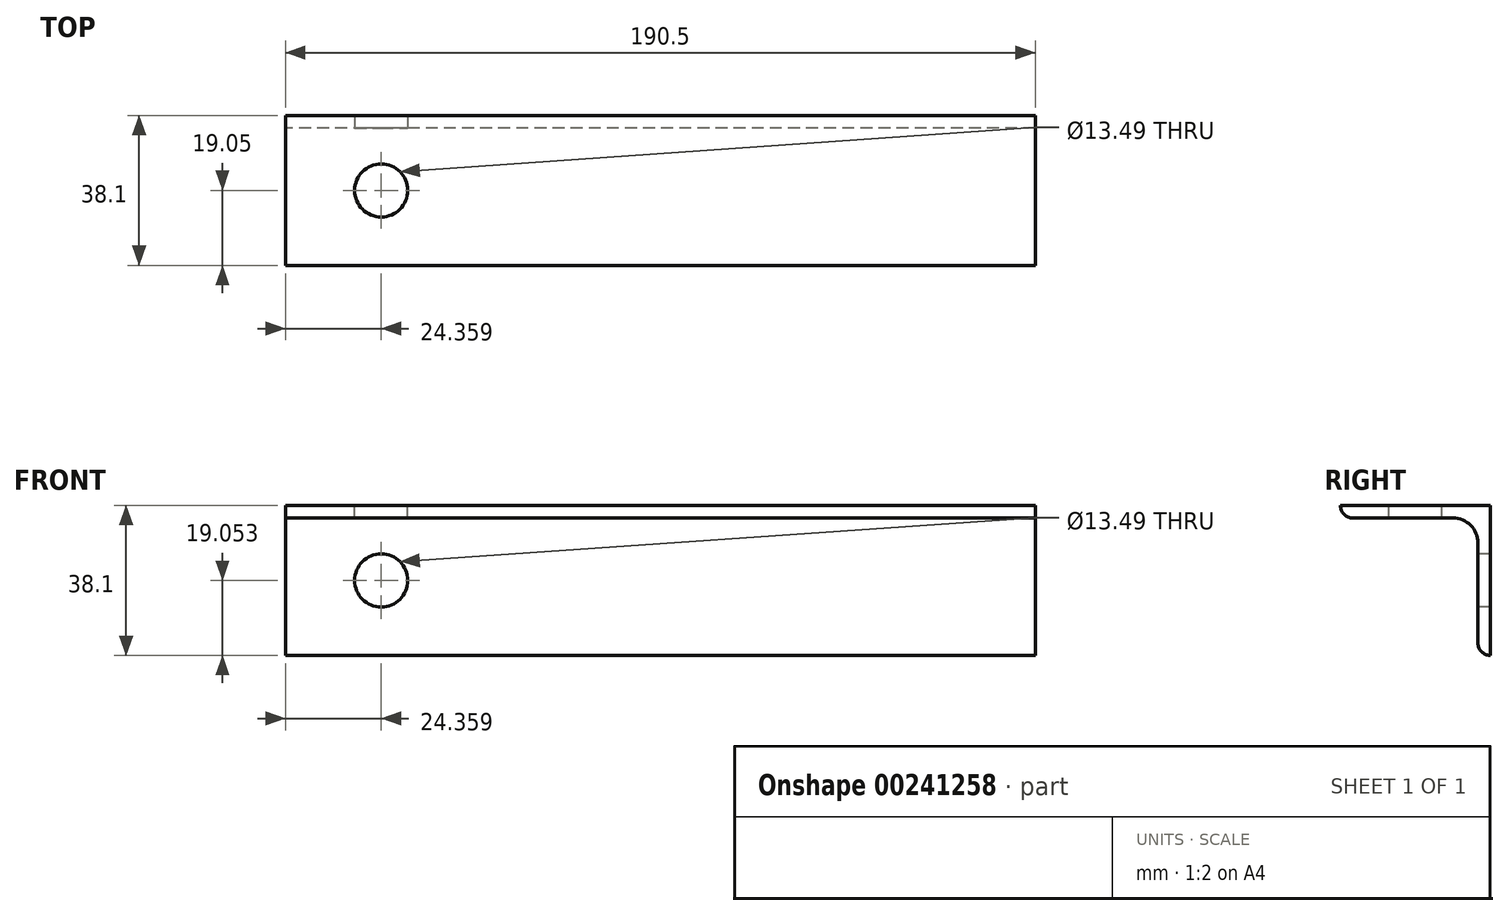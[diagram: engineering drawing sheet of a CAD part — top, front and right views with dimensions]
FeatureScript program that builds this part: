
annotation { "Feature Type Name" : "Feature", "Feature Type Description" : "" }
export const myFeature = defineFeature(function(context is Context, id is Id, definition is map)
    precondition{}
    {
        {
            var Q0;
            Q0=qCreatedBy(makeId("Right.planeOp"),FACE);
            var sketch = newSketch(context, id + "F0", { "sketchPlane" : qUnion([Q0])});
            skLineSegment(sketch, "E0", {"start": v(0, -7.2) * mm, "end": v(0, 30.9) * mm});
            skLineSegment(sketch, "E1", {"start": v(0, 30.9) * mm, "end": v(-38.1, 30.9) * mm});
            skLineSegment(sketch, "E2", {"start": v(-38.1, 30.9) * mm, "end": v(-38.1, 30.9) * mm});
            skLineSegment(sketch, "E3", {"start": v(-34.93, 27.73) * mm, "end": v(-9.52, 27.73) * mm});
            skLineSegment(sketch, "E4", {"start": v(-3.17, 21.38) * mm, "end": v(-3.17, -4.02) * mm});
            skLineSegment(sketch, "E5", {"start": v(-0.1, -7.19) * mm, "end": v(0, -7.2) * mm});
            skPoint(sketch, "E6.visualSharp", {"position": v(-3.17, -7.09) * mm});
            skArc(sketch, "E6.filletArc", {"start": v(-3.17, -4.02) * mm, "mid": v(-2.28, -6.22) * mm, "end": v(-0.1, -7.19) * mm});
            skPoint(sketch, "E7.visualSharp", {"position": v(-38.1, 27.73) * mm});
            skArc(sketch, "E7.filletArc", {"start": v(-38.1, 30.9) * mm, "mid": v(-37.17, 28.66) * mm, "end": v(-34.93, 27.73) * mm});
            skPoint(sketch, "E8.visualSharp", {"position": v(-3.17, 27.73) * mm});
            skArc(sketch, "E8.filletArc", {"start": v(-3.17, 21.38) * mm, "mid": v(-5.03, 25.87) * mm, "end": v(-9.52, 27.73) * mm});
            skSolve(sketch);
        }
        {
            var Q0;
            Q0=makeQuery(id+"F0.imprint","IMPRINT",FACE,{"disambiguationData":[TD([[makeQuery(id+"F0.imprint","IMPRINT",EDGE,{"derivedFrom":sQuery(id+"F0.wireOp",EDGE,"E0")}),1.0]])]});
            extrude(context, id + "F1", {"entities" : qUnion([Q0]), "depth" : 190.5 * mm});
        }
        {
            var Q0;
            Q0=makeQuery(id+"F1.opExtrude","SWEPT_BODY",BODY,{"disambiguationData":[OSD([sQuery(id+"F0.wireOp",EDGE,"E0"),sQuery(id+"F0.wireOp",EDGE,"E1"),sQuery(id+"F0.wireOp",EDGE,"E3"),sQuery(id+"F0.wireOp",EDGE,"E4"),sQuery(id+"F0.wireOp",EDGE,"E5"),sQuery(id+"F0.wireOp",EDGE,"E6.filletArc"),sQuery(id+"F0.wireOp",EDGE,"E7.filletArc"),sQuery(id+"F0.wireOp",EDGE,"E8.filletArc")])]});
            transform(context, id + "F2", {"entities" : qUnion([Q0]), "transformType" : TransformType.TRANSLATION_3D, "dx" : -137.16 * mm, "dy" : 0 * mm, "dz" : 1.52 * mm, "makeCopy" : false});
        }
        {
            var Q0;
            Q0=makeQuery(id+"F1.opExtrude","SWEPT_FACE",FACE,{"disambiguationData":[OSD([sQuery(id+"F0.wireOp",EDGE,"E4")])]});
            var sketch = newSketch(context, id + "F3", { "sketchPlane" : qUnion([Q0])});
            skCircle(sketch, "E9", {"center": v(-112.8, 13.38) * mm, "radius": 6.35 * mm});
            skLineSegment(sketch, "E10", {"start": v(-112.8, 13.38) * mm, "end": v(-137.16, 13.38) * mm});
            skLineSegment(sketch, "E11.bottom", {"start": v(-137.16, 22.9) * mm, "end": v(53.34, 22.9) * mm});
            skLineSegment(sketch, "E11.top", {"start": v(-137.16, -2.5) * mm, "end": v(53.34, -2.5) * mm});
            skLineSegment(sketch, "E11.left", {"start": v(-137.16, 22.9) * mm, "end": v(-137.16, -2.5) * mm});
            skLineSegment(sketch, "E11.right", {"start": v(53.34, 22.9) * mm, "end": v(53.34, -2.5) * mm});
            skSolve(sketch);
        }
        {
            var Q0;
            Q0=makeQuery(id+"F1.opExtrude","SWEPT_FACE",FACE,{"disambiguationData":[OSD([sQuery(id+"F0.wireOp",EDGE,"E1")])]});
            var sketch = newSketch(context, id + "F4", { "sketchPlane" : qUnion([Q0])});
            skCircle(sketch, "E12", {"center": v(-112.8, -19.05) * mm, "radius": 9.24 * mm});
            skSolve(sketch);
        }
        {
            var Q0;
            Q0=sQuery(id+"F4.wireOp",VERTEX,"E12.center");
            var Q1;
            Q1=makeQuery(id+"F1.opExtrude","SWEPT_BODY",BODY,{"disambiguationData":[OSD([sQuery(id+"F0.wireOp",EDGE,"E0"),sQuery(id+"F0.wireOp",EDGE,"E1"),sQuery(id+"F0.wireOp",EDGE,"E3"),sQuery(id+"F0.wireOp",EDGE,"E4"),sQuery(id+"F0.wireOp",EDGE,"E5"),sQuery(id+"F0.wireOp",EDGE,"E6.filletArc"),sQuery(id+"F0.wireOp",EDGE,"E7.filletArc"),sQuery(id+"F0.wireOp",EDGE,"E8.filletArc")])]});
            hole(context, id + "F5", {"style" : HoleStyle.SIMPLE, "endStyle" : HoleEndStyle.THROUGH, "standardTappedOrClearance" : lookupTablePath({ "standard" : "ANSI", "fit" : "Normal (ASME)", "size" : "1/2", "type" : "Clearance" }), "standardBlindInLast" : lookupTablePath({ "fit" : "Free", "standard" : "ANSI", "size" : "1/2", "type" : "Clearance" }), "holeDiameter" : 13.5 * mm, "locations" : qUnion([Q0]), "scope" : qUnion([Q1]), "isTappedThrough" : true});
        }
        {
            var Q0;
            Q0=sQuery(id+"F3.wireOp",VERTEX,"E9.center");
            var Q1;
            Q1=makeQuery(id+"F1.opExtrude","SWEPT_BODY",BODY,{"disambiguationData":[OSD([sQuery(id+"F0.wireOp",EDGE,"E0"),sQuery(id+"F0.wireOp",EDGE,"E1"),sQuery(id+"F0.wireOp",EDGE,"E3"),sQuery(id+"F0.wireOp",EDGE,"E4"),sQuery(id+"F0.wireOp",EDGE,"E5"),sQuery(id+"F0.wireOp",EDGE,"E6.filletArc"),sQuery(id+"F0.wireOp",EDGE,"E7.filletArc"),sQuery(id+"F0.wireOp",EDGE,"E8.filletArc")])]});
            hole(context, id + "F6", {"style" : HoleStyle.SIMPLE, "endStyle" : HoleEndStyle.THROUGH, "standardTappedOrClearance" : lookupTablePath({ "standard" : "ANSI", "fit" : "Normal (ASME)", "size" : "1/2", "type" : "Clearance" }), "standardBlindInLast" : lookupTablePath({ "fit" : "Free", "standard" : "ANSI", "size" : "1/2", "type" : "Clearance" }), "holeDiameter" : 13.5 * mm, "locations" : qUnion([Q0]), "scope" : qUnion([Q1]), "isTappedThrough" : true});
        }
    });
